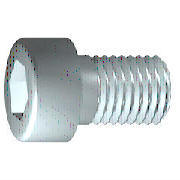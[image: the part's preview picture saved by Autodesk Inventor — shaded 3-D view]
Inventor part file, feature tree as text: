
AUTODESK INVENTOR PART (.ipt)
format: ipt  version: 2015 (Build 190159000, 159)  size: 193,536 bytes
history: native  units: mm (DEFAULTED — no unit token found)
features: sketch x2, extrude x1, plane x1, fillet x1
ambient origin geometry x7: Origin, YZ Plane, XY Plane, X Axis, Y Axis, Z Axis, Center Point
bodies: Solid1 (feature_tree), Body (feature_tree)
feature tree (5):
  extrude  "Slot"  Depth=6.0mm
  plane  "Work Plane1"
  fillet  "Fillet2"  Radius=6.0mm
  sketch  "Sketch1"  dims[d1=27.5mm d2=0.61355mm d3=6.0mm]
  sketch  "Sketch2"  dims[d4=3.0mm d5=60.0deg d6=6.0mm d7=6.0mm d8=5.773503mm d9=10.0mm d10=90.0deg d11=10.0mm d12=0.0mm d13=27.5mm d14=0.0mm d15=0.61345mm d16=0.61345mm d17=0.6mm d19=0.0mm d26=30.0mm d27=45.0deg d28=0.0mm d29=0.0mm d30=0.1mm]
